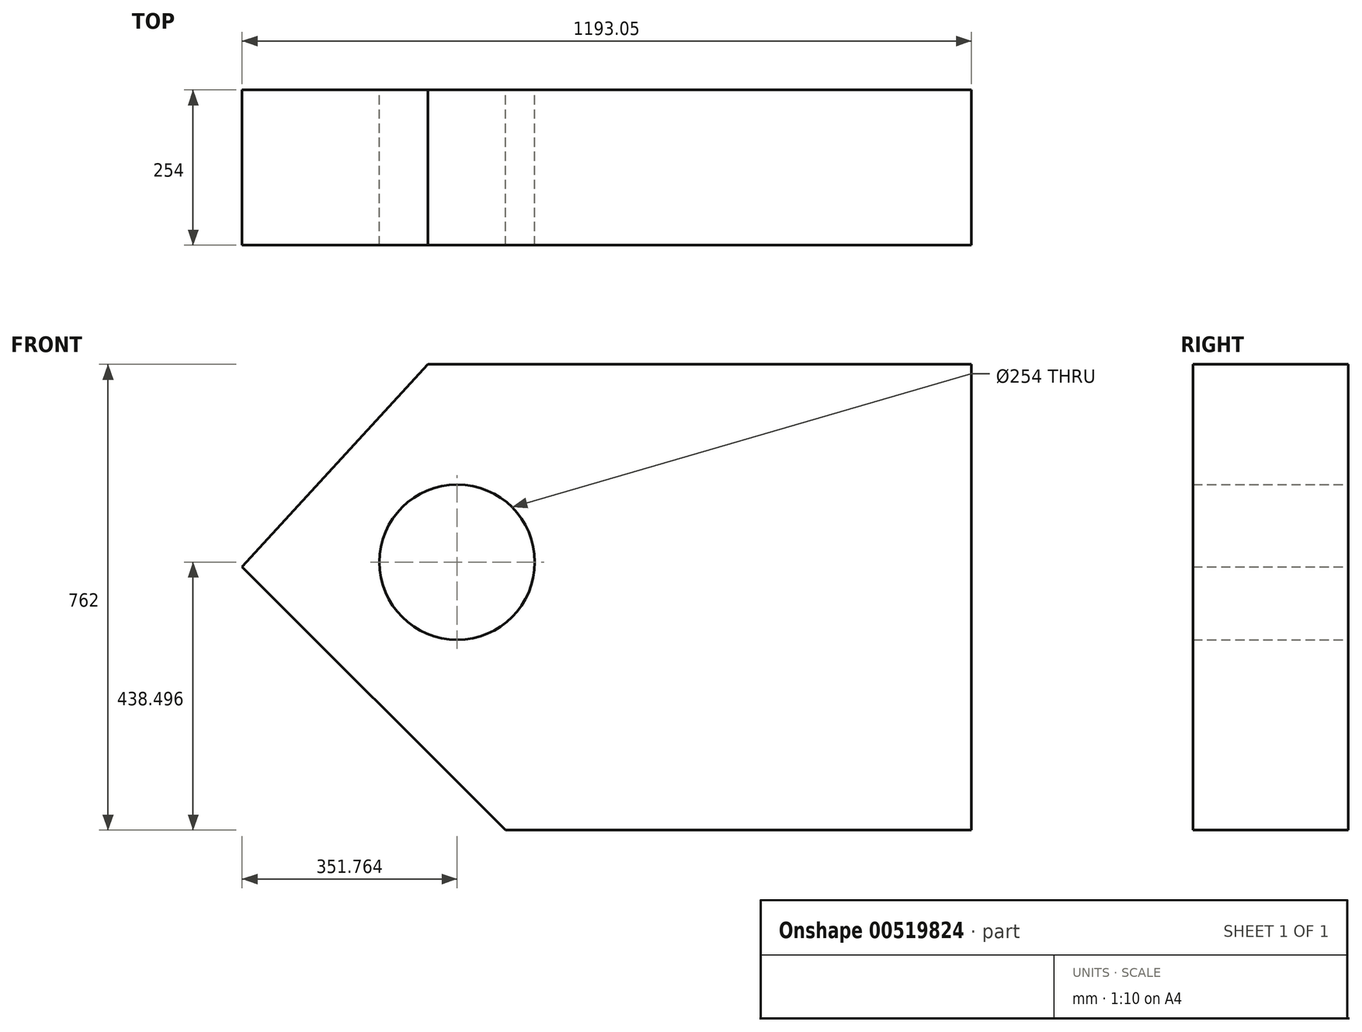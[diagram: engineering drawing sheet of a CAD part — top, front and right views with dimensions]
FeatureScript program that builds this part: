
annotation { "Feature Type Name" : "Feature", "Feature Type Description" : "" }
export const myFeature = defineFeature(function(context is Context, id is Id, definition is map)
    precondition{}
    {
        {
            var Q0;
            Q0=qCreatedBy(makeId("Front.planeOp"),FACE);
            var sketch = newSketch(context, id + "F0", { "sketchPlane" : qUnion([Q0])});
            skLineSegment(sketch, "E0", {"start": v(0, 0) * mm, "end": v(431.05, -431.05) * mm});
            skLineSegment(sketch, "E1", {"start": v(431.05, -431.05) * mm, "end": v(1193.05, -431.05) * mm});
            skLineSegment(sketch, "E2", {"start": v(1193.05, -431.05) * mm, "end": v(1193.05, 330.95) * mm});
            skLineSegment(sketch, "E3", {"start": v(1193.05, 330.95) * mm, "end": v(304.05, 330.95) * mm});
            skLineSegment(sketch, "E4", {"start": v(0, 0) * mm, "end": v(304.05, 330.95) * mm});
            skCircle(sketch, "E5", {"center": v(351.76, 7.45) * mm, "radius": 127 * mm});
            skSolve(sketch);
        }
        {
            var Q0;
            Q0 = qSketchRegion(id + "F0", true);
            extrude(context, id + "F1", {"entities" : qUnion([Q0]), "depth" : 254 * mm, "offsetDistance" : 25.4 * mm});
        }
    });
